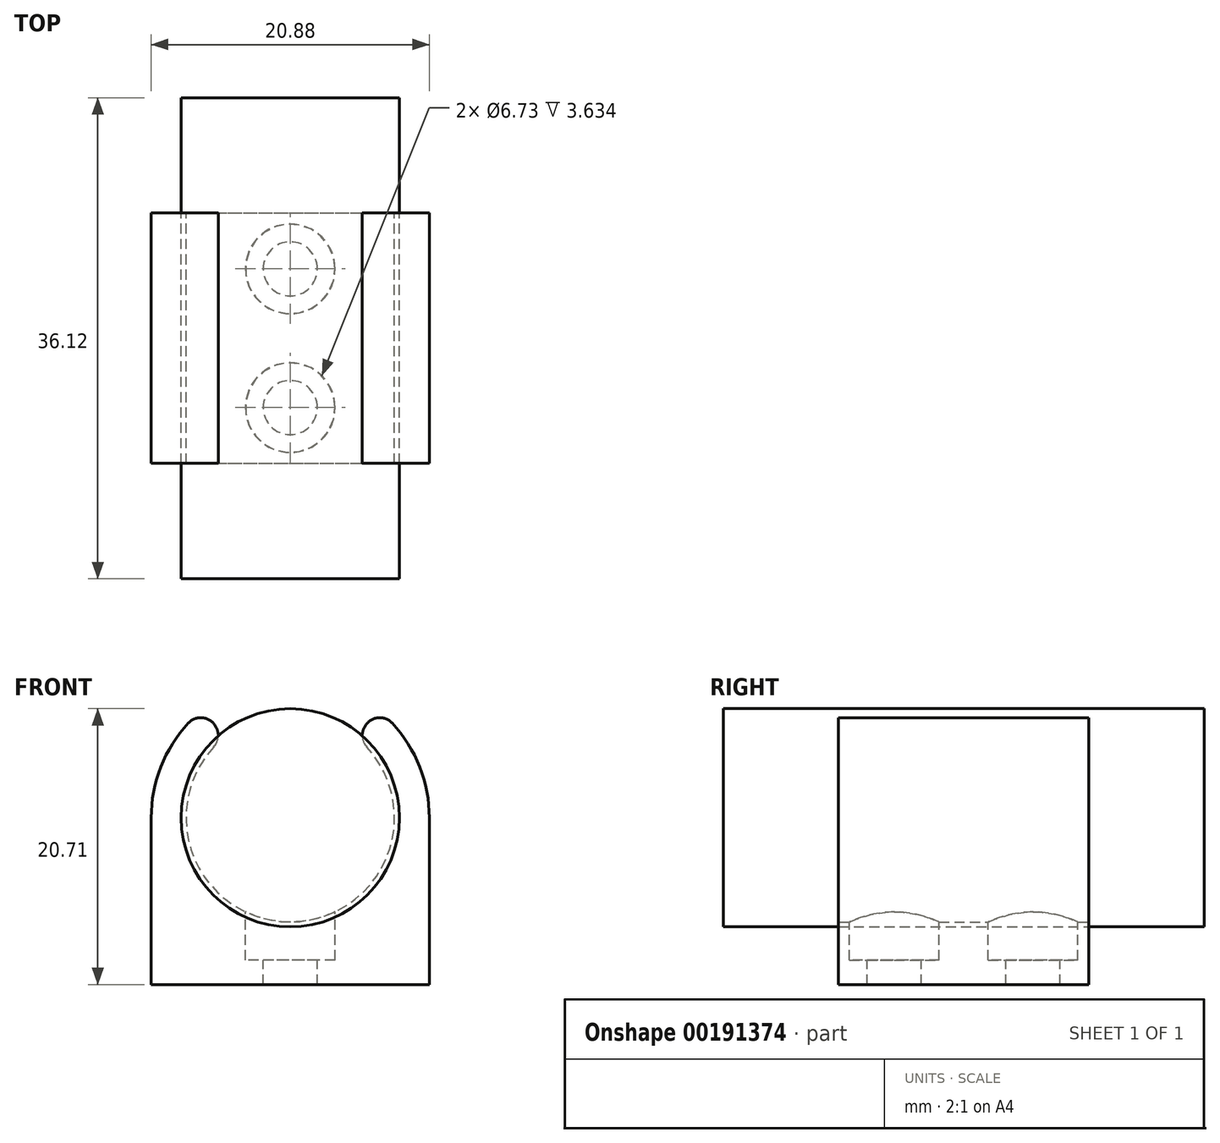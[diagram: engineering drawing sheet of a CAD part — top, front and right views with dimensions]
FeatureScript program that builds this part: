
annotation { "Feature Type Name" : "Feature", "Feature Type Description" : "" }
export const myFeature = defineFeature(function(context is Context, id is Id, definition is map)
    precondition{}
    {
        {
            var Q0;
            Q0=qCreatedBy(makeId("Front.planeOp"),FACE);
            var sketch = newSketch(context, id + "F0", { "sketchPlane" : qUnion([Q0])});
            skArc(sketch, "E0", {"start": v(10.44, 0) * mm, "mid": v(9.72, 3.82) * mm, "end": v(7.65, 7.1) * mm});
            skArc(sketch, "E1", {"start": v(-5.74, 5.31) * mm, "mid": v(0, -7.82) * mm, "end": v(5.74, 5.31) * mm});
            skLineSegment(sketch, "E2", {"start": v(-10.44, 0) * mm, "end": v(-10.44, -12.52) * mm});
            skLineSegment(sketch, "E3", {"start": v(-10.44, -12.52) * mm, "end": v(10.44, -12.52) * mm});
            skLineSegment(sketch, "E4", {"start": v(10.44, -12.52) * mm, "end": v(10.44, 0) * mm});
            skLineSegment(sketch, "E5", {"start": v(0, 29.99) * mm, "end": v(0, -32.46) * mm, "construction": true});
            skLineSegment(sketch, "E6", {"start": v(-5.58, 6.8) * mm, "end": v(-5.62, 6.88) * mm});
            skLineSegment(sketch, "E7", {"start": v(5.58, 6.8) * mm, "end": v(5.62, 6.88) * mm});
            skArc(sketch, "E8.trimOffspring", {"start": v(-7.65, 7.1) * mm, "mid": v(-9.72, 3.82) * mm, "end": v(-10.44, 0) * mm});
            skPoint(sketch, "E9.visualSharp", {"position": v(-5.08, 5.95) * mm});
            skArc(sketch, "E9.filletArc", {"start": v(-5.74, 5.31) * mm, "mid": v(-5.41, 6.03) * mm, "end": v(-5.58, 6.8) * mm});
            skPoint(sketch, "E10.visualSharp", {"position": v(5.08, 5.95) * mm});
            skArc(sketch, "E10.filletArc", {"start": v(5.58, 6.8) * mm, "mid": v(5.41, 6.03) * mm, "end": v(5.74, 5.31) * mm});
            skPoint(sketch, "E11.visualSharp", {"position": v(-6.4, 8.24) * mm});
            skArc(sketch, "E11.filletArc", {"start": v(-5.62, 6.88) * mm, "mid": v(-6.57, 7.5) * mm, "end": v(-7.65, 7.1) * mm});
            skPoint(sketch, "E12.visualSharp", {"position": v(6.4, 8.24) * mm});
            skArc(sketch, "E12.filletArc", {"start": v(7.65, 7.1) * mm, "mid": v(6.57, 7.5) * mm, "end": v(5.62, 6.88) * mm});
            skSolve(sketch);
        }
        {
            var Q0;
            Q0 = qSketchRegion(id + "F0", true);
            extrude(context, id + "F1", {"entities" : qUnion([Q0]), "endBound" : BoundingType.SYMMETRIC, "depth" : 18.8 * mm});
        }
        {
            var Q0;
            Q0=qCreatedBy(makeId("Top.planeOp"),FACE);
            var sketch = newSketch(context, id + "F2", { "sketchPlane" : qUnion([Q0])});
            skCircle(sketch, "E13", {"center": v(0, 5.2) * mm, "radius": 2.03 * mm});
            skCircle(sketch, "E14", {"center": v(0, -5.2) * mm, "radius": 2.03 * mm});
            skSolve(sketch);
        }
        {
            var Q0;
            Q0 = qSketchRegion(id + "F2", true);
            extrude(context, id + "F3", {"entities" : qUnion([Q0]), "operationType" : NewBodyOperationType.REMOVE, "endBound" : BoundingType.THROUGH_ALL, "oppositeDirection" : true, "depth" : 25.4 * mm});
        }
        {
            var Q0;
            Q0=qCreatedBy(makeId("Top.planeOp"),FACE);
            var sketch = newSketch(context, id + "F4", { "sketchPlane" : qUnion([Q0])});
            skCircle(sketch, "E15", {"center": v(0, 5.2) * mm, "radius": 3.37 * mm});
            skCircle(sketch, "E16", {"center": v(0, -5.2) * mm, "radius": 3.37 * mm});
            skSolve(sketch);
        }
        {
            var Q0;
            Q0 = qSketchRegion(id + "F4", true);
            extrude(context, id + "F5", {"entities" : qUnion([Q0]), "operationType" : NewBodyOperationType.REMOVE, "oppositeDirection" : true, "depth" : 10.7 * mm});
        }
        {
            var Q0;
            Q0=qCreatedBy(makeId("Front.planeOp"),FACE);
            var sketch = newSketch(context, id + "F6", { "sketchPlane" : qUnion([Q0])});
            skCircle(sketch, "E17", {"center": v(0, 0) * mm, "radius": 8.2 * mm});
            skSolve(sketch);
        }
        {
            var Q0;
            Q0 = qSketchRegion(id + "F6", true);
            extrude(context, id + "F7", {"entities" : qUnion([Q0]), "endBound" : BoundingType.SYMMETRIC, "depth" : 36.12 * mm});
        }
        {
            var Q0;
            Q0=qCreatedBy(makeId("Front.planeOp"),FACE);
            var sketch = newSketch(context, id + "F8", { "sketchPlane" : qUnion([Q0])});
            skCircle(sketch, "E18", {"center": v(-29, 47.18) * mm, "radius": 1.71 * mm});
            skCircle(sketch, "E19", {"center": v(0, 47.18) * mm, "radius": 1.71 * mm});
            skCircle(sketch, "E20", {"center": v(0, 18.18) * mm, "radius": 1.71 * mm});
            skCircle(sketch, "E21", {"center": v(-29, 18.18) * mm, "radius": 1.71 * mm});
            skLineSegment(sketch, "E22.bottom", {"start": v(-32.17, 50.36) * mm, "end": v(3.18, 50.36) * mm});
            skLineSegment(sketch, "E22.top", {"start": v(-32.17, 15) * mm, "end": v(3.18, 15) * mm});
            skLineSegment(sketch, "E22.left", {"start": v(-32.17, 50.36) * mm, "end": v(-32.17, 15) * mm});
            skLineSegment(sketch, "E22.right", {"start": v(3.18, 50.36) * mm, "end": v(3.18, 15) * mm});
            skSolve(sketch);
        }
        {
            var Q0;
            Q0 = qSketchRegion(id + "F8", true);
            extrude(context, id + "F9", {"entities" : qUnion([Q0]), "depth" : .6 * mm});
        }
        {
            var Q0;
            Q0=makeQuery(id+"F9.opExtrude","SWEPT_BODY",BODY,{"disambiguationData":[OSD([sQuery(id+"F8.wireOp",EDGE,"E18"),sQuery(id+"F8.wireOp",EDGE,"E19"),sQuery(id+"F8.wireOp",EDGE,"E20"),sQuery(id+"F8.wireOp",EDGE,"E21"),sQuery(id+"F8.wireOp",EDGE,"E22.bottom"),sQuery(id+"F8.wireOp",EDGE,"E22.top"),sQuery(id+"F8.wireOp",EDGE,"E22.left"),sQuery(id+"F8.wireOp",EDGE,"E22.right")])]});
            deleteBodies(context, id + "F10", {"entities" : qUnion([Q0])});
        }
    });
